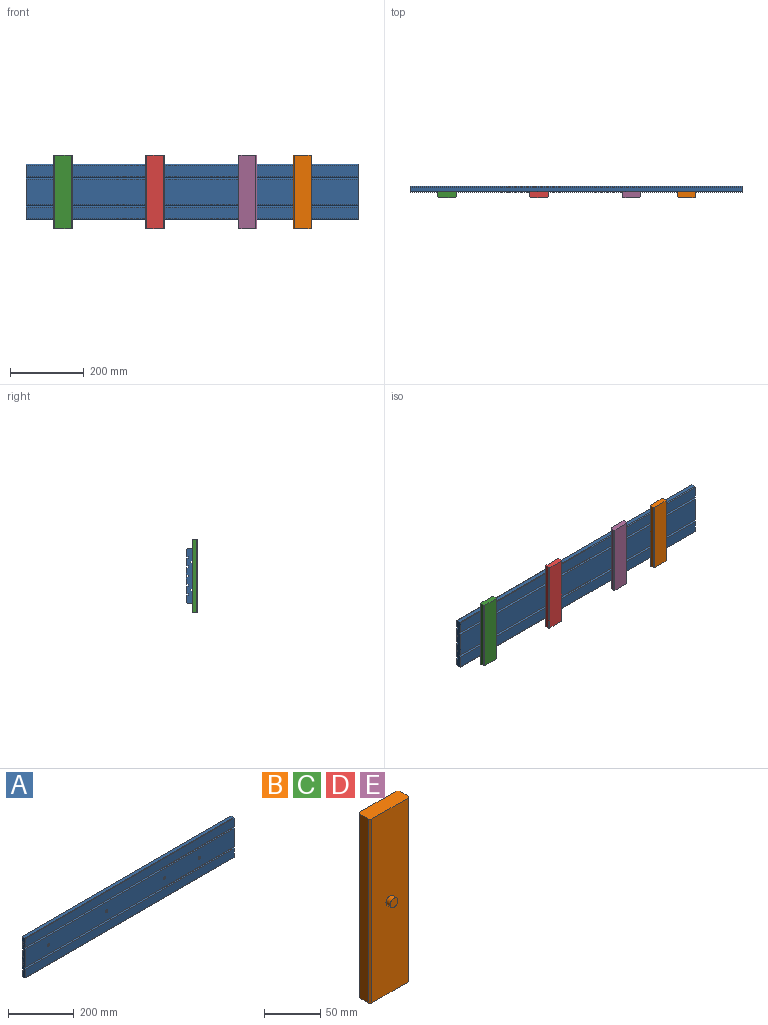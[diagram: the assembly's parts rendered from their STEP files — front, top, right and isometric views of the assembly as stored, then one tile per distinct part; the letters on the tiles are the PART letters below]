
ASSEMBLY  parts=5 mates=7
PART A: 44 faces, bbox 900x15x150 mm
  f0: plane 900x20.5mm, normal (0,1,0), area 18450mm2, adj f5,f6,f35,f42
  f1: plane 900x20mm, normal (0,1,0), area 18000mm2, adj f5,f6,f33,f37
  f2: plane 900x20mm, normal (0,1,0), area 18000mm2, adj f5,f6,f30,f32
  f3: plane 900x20mm, normal (0,1,0), area 18000mm2, adj f5,f6,f27,f29
  f4: plane 900x20mm, normal (0,1,0), area 18000mm2, adj f5,f6,f24,f26
  f5: plane 150x15mm, normal (-1,0,0), area 2092mm2, adj f0,f1,f2,f3,f4,f7,f8,f9
  f6: plane 150x15mm, normal (1,0,0), area 2092mm2, adj f0,f1,f2,f3,f4,f7,f8,f9
  f7: plane 900x67.93mm, normal (0,-1,0), area 60821.9mm2, adj f5,f6,f13,f15,f17,f19,f21,f39
  f8: plane 900x31.96mm, normal (0,-1,0), area 28768mm2, adj f5,f6,f38,f41
  f9: plane 900x31.96mm, normal (0,-1,0), area 28768mm2, adj f5,f6,f22,f43
  f10: plane 900x11mm, normal (0,0,-1), area 9900mm2, adj f5,f6,f40,f41
  f11: plane 900x11mm, normal (0,0,1), area 9900mm2, adj f5,f6,f42,f43
  f12: plane 900x20.5mm, normal (0,1,0), area 18450mm2, adj f5,f6,f23,f40
  f13: cylinder r=5mm len=10mm, axis (0,-1,0), area 157.1mm2, adj f7,f14
  f14: plane 10x10mm, normal (0,-1,0), area 78.5mm2, adj f13
  f15: cylinder r=5mm len=10mm, axis (0,-1,0), area 157.1mm2, adj f7,f16
  f16: plane 10x10mm, normal (0,-1,0), area 78.5mm2, adj f15
  f17: cylinder r=5mm len=10mm, axis (0,-1,0), area 157.1mm2, adj f7,f18
  f18: plane 10x10mm, normal (0,-1,0), area 78.5mm2, adj f17
  f19: cylinder r=5mm len=10mm, axis (0,-1,0), area 157.1mm2, adj f7,f20
  f20: plane 10x10mm, normal (0,-1,0), area 78.5mm2, adj f19
  f21: plane 900x3.54mm, normal (0,-0.71,0.71), area 4500mm2, adj f5,f6,f7,f22
  f22: plane 900x3.54mm, normal (0,-0.71,-0.71), area 4500mm2, adj f5,f6,f9,f21
  f23: plane 900x5mm, normal (0,0,1), area 4500mm2, adj f5,f6,f12,f25
  f24: plane 900x5mm, normal (0,0,-1), area 4500mm2, adj f4,f5,f6,f25
  f25: plane 900x5mm, normal (0,1,0), area 4500mm2, adj f5,f6,f23,f24
  f26: plane 900x5mm, normal (0,0,1), area 4500mm2, adj f4,f5,f6,f28
  f27: plane 900x5mm, normal (0,0,-1), area 4500mm2, adj f3,f5,f6,f28
  f28: plane 900x5mm, normal (0,1,0), area 4500mm2, adj f5,f6,f26,f27
  f29: plane 900x5mm, normal (0,0,1), area 4500mm2, adj f3,f5,f6,f31
  f30: plane 900x5mm, normal (0,0,-1), area 4500mm2, adj f2,f5,f6,f31
  f31: plane 900x5mm, normal (0,1,0), area 4500mm2, adj f5,f6,f29,f30
  f32: plane 900x5mm, normal (0,0,1), area 4500mm2, adj f2,f5,f6,f34
  f33: plane 900x5mm, normal (0,0,-1), area 4500mm2, adj f1,f5,f6,f34
  f34: plane 900x5mm, normal (0,1,0), area 4500mm2, adj f5,f6,f32,f33
  f35: plane 900x5mm, normal (0,0,-1), area 4500mm2, adj f0,f5,f6,f36
  f36: plane 900x5mm, normal (0,1,0), area 4500mm2, adj f5,f6,f35,f37
  f37: plane 900x5mm, normal (0,0,1), area 4500mm2, adj f1,f5,f6,f36
  f38: plane 900x3.54mm, normal (0,-0.71,0.71), area 4500mm2, adj f5,f6,f8,f39
  f39: plane 900x3.54mm, normal (0,-0.71,-0.71), area 4500mm2, adj f5,f6,f7,f38
  f40: plane 900x2mm, normal (0,0.71,-0.71), area 2545.6mm2, adj f5,f6,f10,f12
  f41: plane 900x2mm, normal (0,-0.71,-0.71), area 2545.6mm2, adj f5,f6,f8,f10
  f42: plane 900x2mm, normal (0,0.71,0.71), area 2545.6mm2, adj f0,f5,f6,f11
  f43: plane 900x2mm, normal (0,-0.71,0.71), area 2545.6mm2, adj f5,f6,f9,f11
PART B: 12 faces, bbox 50x20x200 mm
  f0: plane 200x11mm, normal (-1,0,0), area 2200mm2, adj f1,f3,f8,f11
  f1: plane 50x15mm, normal (0,0,-1), area 742mm2, adj f0,f2,f4,f5,f8,f9,f10,f11
  f2: plane 200x11mm, normal (1,0,0), area 2200mm2, adj f1,f3,f9,f10
  f3: plane 50x15mm, normal (0,0,1), area 742mm2, adj f0,f2,f4,f5,f8,f9,f10,f11
  f4: plane 200x46mm, normal (0,-1,0), area 9121.5mm2, adj f1,f3,f6,f10,f11
  f5: plane 200x46mm, normal (0,1,0), area 9200mm2, adj f1,f3,f8,f9
  f6: cylinder r=5mm len=10mm, axis (0,1,0), area 157.1mm2, adj f4,f7
  f7: plane 10x10mm, normal (0,-1,0), area 78.5mm2, adj f6
  f8: plane 200x2mm, normal (-0.71,0.71,0), area 565.7mm2, adj f0,f1,f3,f5
  f9: plane 200x2mm, normal (0.71,0.71,0), area 565.7mm2, adj f1,f2,f3,f5
  f10: plane 200x2mm, normal (0.71,-0.71,0), area 565.7mm2, adj f1,f2,f3,f4
  f11: plane 200x2mm, normal (-0.71,-0.71,0), area 565.7mm2, adj f0,f1,f3,f4
PART C: same geometry as B
PART D: same geometry as B
PART E: same geometry as B
PLACE A t=(-2.01,7.02,1.02)mm fixed
PLACE B rot(axis=(1,0,0),180deg) t=(297.99,-22.98,1.02)mm
PLACE C rot(axis=(1,0,0),180deg) t=(-352.01,-22.98,1.02)mm
PLACE D rot(axis=(1,0,0),180deg) t=(-102.01,-22.98,1.02)mm
PLACE E rot(axis=(1,0,0),180deg) t=(147.99,-22.98,1.02)mm
MATE planar A.f7 <-> B.f4  axis (0,-1,0) through (-2.01,-7.98,1.02)mm
MATE planar C.f4 <-> A.f7  axis (0,1,0) through (-352.01,-7.98,-98.98)mm
MATE planar E.f4 <-> A.f7  axis (0,1,0) through (147.99,-7.98,-98.98)mm
MATE cylindrical B.f6 <-> A.f19  axis (0,1,0) through (297.99,-7.98,1.02)mm
MATE cylindrical E.f6 <-> A.f13  axis (0,1,0) through (147.99,-7.98,1.02)mm
MATE cylindrical A.f15 <-> C.f6  axis (0,-1,0) through (-352.01,-7.98,1.02)mm
MATE cylindrical A.f17 <-> D.f6  axis (0,-1,0) through (-102.01,-7.98,1.02)mm
